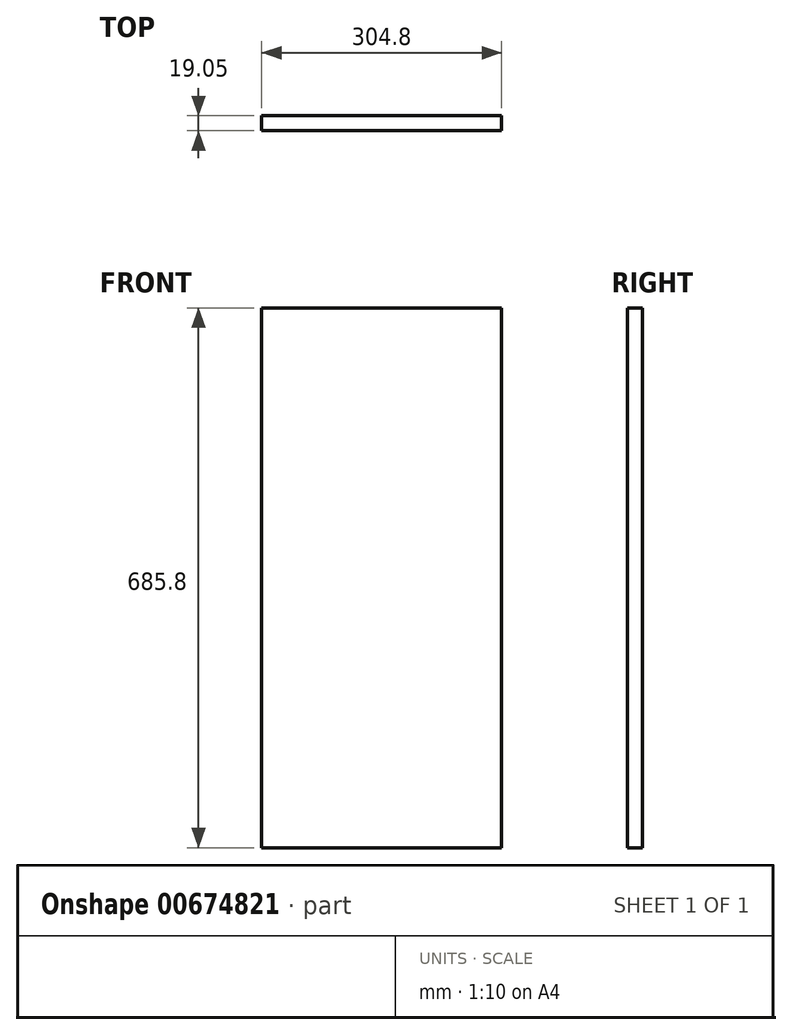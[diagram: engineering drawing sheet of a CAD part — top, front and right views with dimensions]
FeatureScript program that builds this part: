
annotation { "Feature Type Name" : "Feature", "Feature Type Description" : "" }
export const myFeature = defineFeature(function(context is Context, id is Id, definition is map)
    precondition{}
    {
        {
            var Q0;
            Q0=qCreatedBy(makeId("Front.planeOp"),FACE);
            var sketch = newSketch(context, id + "F0", { "sketchPlane" : qUnion([Q0])});
            skLineSegment(sketch, "E0.bottom", {"start": v(-152.4, 342.9) * mm, "end": v(152.4, 342.9) * mm});
            skLineSegment(sketch, "E0.top", {"start": v(-152.4, -342.9) * mm, "end": v(152.4, -342.9) * mm});
            skLineSegment(sketch, "E0.left", {"start": v(-152.4, 342.9) * mm, "end": v(-152.4, -342.9) * mm});
            skLineSegment(sketch, "E0.right", {"start": v(152.4, 342.9) * mm, "end": v(152.4, -342.9) * mm});
            skPoint(sketch, "E0.middle", {"position": v(0, 0) * mm});
            skPoint(sketch, "E1.middle", {"position": v(0, 342.9) * mm});
            skSolve(sketch);
        }
        {
            var Q0;
            Q0=makeQuery(id+"F0.imprint","IMPRINT",FACE,{"disambiguationData":[TD([[makeQuery(id+"F0.imprint","IMPRINT",EDGE,{"derivedFrom":sQuery(id+"F0.wireOp",EDGE,"E0.top")}),1.0]])]});
            extrude(context, id + "F1", {"entities" : qUnion([Q0]), "depth" : 19.05 * mm, "offsetDistance" : 25.4 * mm});
        }
    });
